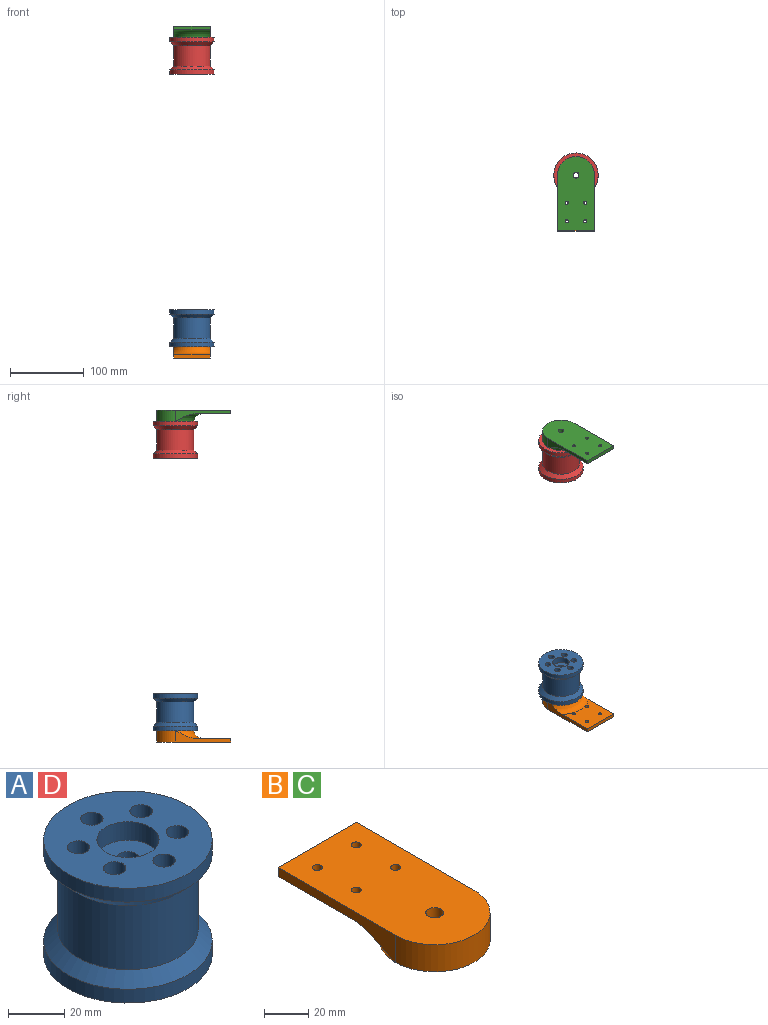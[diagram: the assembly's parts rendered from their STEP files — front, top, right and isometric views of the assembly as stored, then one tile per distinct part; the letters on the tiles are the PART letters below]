
ASSEMBLY  parts=4 mates=3
PART A: 18 faces, bbox 60x60x50 mm
  f0: cylinder r=30mm len=60mm, axis (0,0,1), area 1131mm2, adj f10,f17
  f1: cylinder r=4mm len=34mm, axis (0,0,1), area 854.5mm2, adj f12,f14
  f2: cylinder r=4mm len=50mm, axis (0,0,1), area 1256.6mm2, adj f9,f10
  f3: cylinder r=4mm len=50mm, axis (0,0,1), area 1256.6mm2, adj f9,f10
  f4: cylinder r=4mm len=50mm, axis (0,0,1), area 1256.6mm2, adj f9,f10
  f5: cylinder r=4mm len=50mm, axis (0,0,1), area 1256.6mm2, adj f9,f10
  f6: cylinder r=4mm len=50mm, axis (0,0,1), area 1256.6mm2, adj f9,f10
  f7: cylinder r=4mm len=50mm, axis (0,0,1), area 1256.6mm2, adj f9,f10
  f8: cylinder r=30mm len=60mm, axis (0,0,1), area 1131mm2, adj f9,f16
  f9: plane 60x60mm, normal (0,0,-1), area 2142.2mm2, adj f2,f3,f4,f5,f6,f7,f8,f13
  f10: plane 60x60mm, normal (0,0,1), area 2142.2mm2, adj f0,f2,f3,f4,f5,f6,f7,f11
  f11: cylinder r=11.05mm len=22.1mm, axis (0,0,1), area 555.4mm2, adj f10,f12
  f12: plane 22.1x22.1mm, normal (0,0,1), area 333.3mm2, adj f1,f11
  f13: cylinder r=11.05mm len=22.1mm, axis (0,0,1), area 555.4mm2, adj f9,f14
  f14: plane 22.1x22.1mm, normal (0,0,-1), area 333.3mm2, adj f1,f13
  f15: cylinder r=25mm len=50mm, axis (0,0,1), area 4398.2mm2, adj f16,f17
  f16: cone r=25mm half-angle=45deg, axis (0,0,-1), area 1221.8mm2, adj f8,f15
  f17: cone r=30mm half-angle=45deg, axis (0,0,1), area 1221.8mm2, adj f0,f15
PART B: 13 faces, bbox 79.7x100x17 mm
  f0: plane 50x5mm, normal (0,1,0), area 250mm2, adj f1,f5,f7,f8
  f1: plane 75x15mm, normal (-1,0,0), area 485.8mm2, adj f0,f7,f8,f9,f12
  f2: cylinder r=2.25mm len=5mm, axis (0,0,-1), area 70.7mm2, adj f7,f8
  f3: cylinder r=2.25mm len=5mm, axis (0,0,-1), area 70.7mm2, adj f7,f8
  f4: cylinder r=2.25mm len=5mm, axis (0,0,-1), area 70.7mm2, adj f7,f8
  f5: plane 75x15mm, normal (1,0,0), area 485.8mm2, adj f0,f7,f8,f9,f12
  f6: cylinder r=2.25mm len=5mm, axis (0,0,-1), area 70.7mm2, adj f7,f8
  f7: plane 100x50mm, normal (0,0,1), area 4617.9mm2, adj f0,f1,f2,f3,f4,f5,f6,f9
  f8: plane 50x47.95mm, normal (0,0,-1), area 1998.1mm2, adj f0,f1,f2,f3,f4,f5,f6,f12
  f9: cylinder r=25mm len=50mm, axis (0,0,-1), area 1178.1mm2, adj f1,f5,f7,f11
  f10: cylinder r=4mm len=15mm, axis (0,0,-1), area 377mm2, adj f7,f11
  f11: plane 50x50mm, normal (0,0,-1), area 1913.2mm2, adj f9,f10,f12
  f12: torus R=36.83mm, axis (0,0,1), area 1040.5mm2, adj f1,f5,f8,f11
PART C: same geometry as B
PART D: same geometry as A
PLACE A t=(64.68,96.01,-360.73)mm
PLACE B rot(axis=(1,0,0),180deg) t=(64.68,96.01,-431.23)mm
PLACE C rot(axis=(0,0,-1),180deg) t=(64.68,96.01,8.77)mm fixed
PLACE D t=(64.68,96.01,8.27)mm
MATE revolute B.f10 <-> A.f11  axis (0,0,1) through (64.68,96.01,-421.23)mm
MATE fastened C.f9 <-> B.f10  axis (0,0,1) through (64.68,96.01,13.77)mm
MATE revolute C.f10 <-> D.f11  axis (0,0,-1) through (64.68,96.01,-1.23)mm
